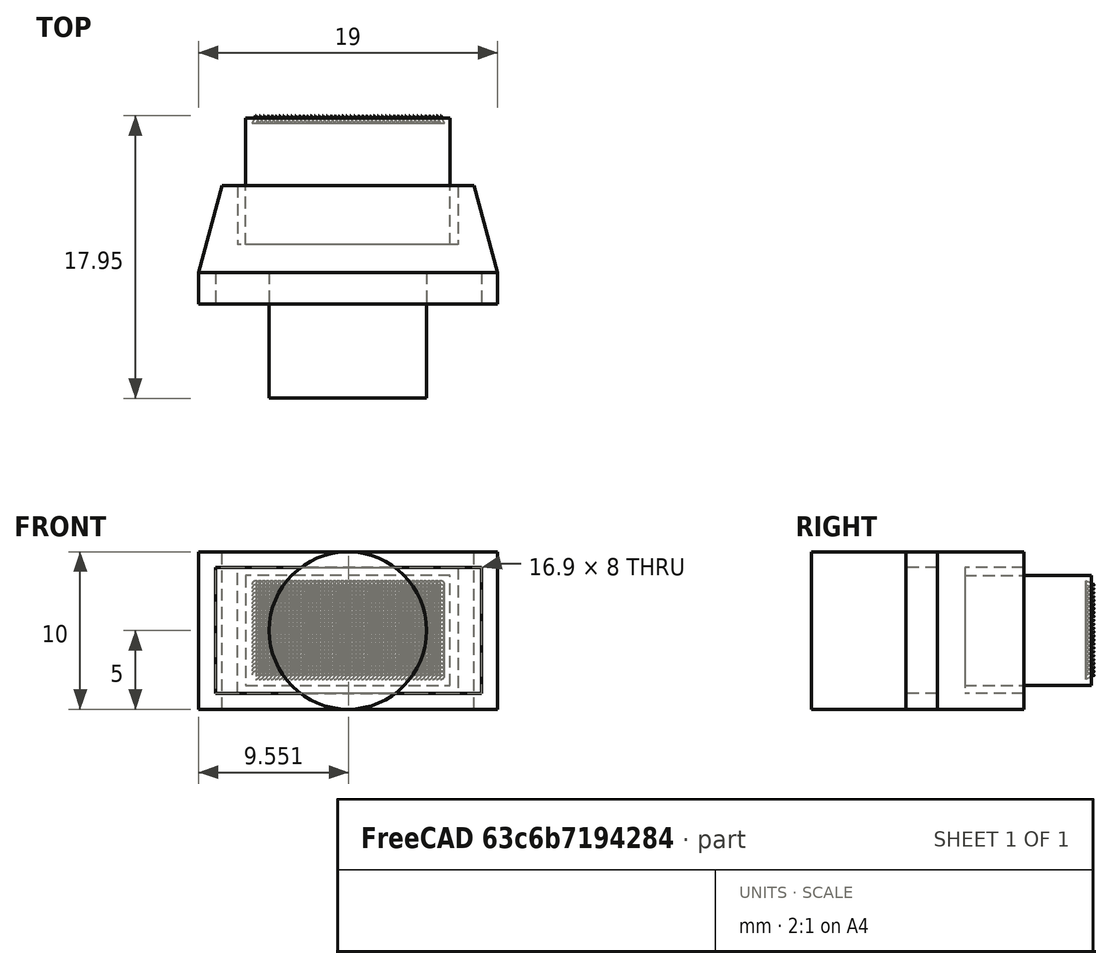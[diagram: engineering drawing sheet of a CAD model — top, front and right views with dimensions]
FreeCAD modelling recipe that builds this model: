
FCSTD DOCUMENT  (FreeCAD 0.18R16110 (Git))
Label: Miyama DS-462
License: All rights reserved
LicenseURL: http://en.wikipedia.org/wiki/All_rights_reserved
objects: Sketcher::SketchObject×8, Part::Extrusion×5, Part::Cut×2, Part::Cone×1, Part::FeaturePython×1, Part::Sweep×1
note: 18 computed .brp shape members not serialized (recipe doc carries the construction recipe); baked Part::Feature solids carry a one-line shape summary decoded from their .brp

FEATURE [Sketcher::SketchObject] Sketch
  sketch-geometry (12):
    g0: LineSegment [constr] StartX=-7 StartY=11.8 StartZ=0 EndX=7 EndY=11.8 EndZ=0
    g1: LineSegment [constr] StartX=-9.5 StartY=0 StartZ=0 EndX=9.5 EndY=0 EndZ=0
    g2: LineSegment [constr] StartX=-7 StartY=11.8 StartZ=0 EndX=-7 EndY=7.5 EndZ=0
    g3: LineSegment [constr] StartX=7 StartY=7.5 StartZ=0 EndX=7 EndY=11.8 EndZ=0
    g4: LineSegment [constr] StartX=9.5 StartY=0 StartZ=0 EndX=9.5 EndY=2 EndZ=0
    g5: LineSegment [constr] StartX=9.5 StartY=2 StartZ=0 EndX=7 EndY=7.5 EndZ=0
    g6: LineSegment [constr] StartX=-9.5 StartY=0 StartZ=0 EndX=-9.5 EndY=2 EndZ=0
    g7: LineSegment [constr] StartX=-9.5 StartY=2 StartZ=0 EndX=-7 EndY=7.5 EndZ=0
    g8: LineSegment StartX=-9.5 StartY=2 StartZ=0 EndX=-9.5 EndY=0 EndZ=0
    g9: LineSegment StartX=-9.5 StartY=0 StartZ=0 EndX=9.5 EndY=0 EndZ=0
    g10: LineSegment StartX=9.5 StartY=0 StartZ=0 EndX=9.5 EndY=2 EndZ=0
    g11: LineSegment StartX=9.5 StartY=2 StartZ=0 EndX=-9.5 EndY=2 EndZ=0
  constraints (31):
    c: DistanceX(g0,g0) = 14
    c: DistanceX(g1,g1) = 19
    c: Symmetric(g0,g0,g-2)
    c: Coincident(g2,g0)
    c: Vertical(g2)
    c: Coincident(g3,g0)
    c: Vertical(g3)
    c: DistanceY(g3,g3) = 4.3
    c: Coincident(g4,g1)
    c: Coincident(g5,g4)
    c: Coincident(g7,g6)
    c: Coincident(g7,g2)
    c: Vertical(g6)
    c: Vertical(g4)
    c: DistanceY(g1,g5) = 7.5
    c: Equal(g4,g6)
    c: Coincident(g6,g1)
    c: DistanceY(g4,g4) = 2
    c: PointOnObject(g-1,g1)
    c: Horizontal(g1)
    c: Equal(g7,g5)
    c: Coincident(g3,g5)
    c: Equal(g3,g2)
    c: Coincident(g6,g8)
    c: Coincident(g8,g1)
    c: Coincident(g8,g9)
    c: Coincident(g9,g1)
    c: Coincident(g9,g10)
    c: Coincident(g10,g4)
    c: Coincident(g10,g11)
    c: Coincident(g11,g8)
FEATURE [Sketcher::SketchObject] Sketch001
  sketch-geometry (12):
    g0: LineSegment [constr] StartX=-8 StartY=11.8 StartZ=0 EndX=8 EndY=11.8 EndZ=0
    g1: LineSegment [constr] StartX=-9.5 StartY=0 StartZ=0 EndX=9.5 EndY=0 EndZ=0
    g2: LineSegment [constr] StartX=-8 StartY=11.8 StartZ=0 EndX=-8 EndY=7.5 EndZ=0
    g3: LineSegment [constr] StartX=8 StartY=7.5 StartZ=0 EndX=8 EndY=11.8 EndZ=0
    g4: LineSegment [constr] StartX=9.5 StartY=0 StartZ=0 EndX=9.5 EndY=2 EndZ=0
    g5: LineSegment [constr] StartX=9.5 StartY=2 StartZ=0 EndX=8 EndY=7.5 EndZ=0
    g6: LineSegment [constr] StartX=-9.5 StartY=0 StartZ=0 EndX=-9.5 EndY=2 EndZ=0
    g7: LineSegment [constr] StartX=-9.5 StartY=2 StartZ=0 EndX=-8 EndY=7.5 EndZ=0
    g8: LineSegment StartX=-9.5 StartY=2 StartZ=0 EndX=-8 EndY=7.5 EndZ=0
    g9: LineSegment StartX=-8 StartY=7.5 StartZ=0 EndX=8 EndY=7.5 EndZ=0
    g10: LineSegment StartX=8 StartY=7.5 StartZ=0 EndX=9.5 EndY=2 EndZ=0
    g11: LineSegment StartX=9.5 StartY=2 StartZ=0 EndX=-9.5 EndY=2 EndZ=0
  constraints (31):
    c: DistanceX(g0,g0) = 16
    c: DistanceX(g1,g1) = 19
    c: Symmetric(g0,g0,g-2)
    c: Coincident(g2,g0)
    c: Vertical(g2)
    c: Coincident(g3,g0)
    c: Vertical(g3)
    c: DistanceY(g3,g3) = 4.3
    c: Coincident(g4,g1)
    c: Coincident(g5,g4)
    c: Coincident(g7,g6)
    c: Coincident(g7,g2)
    c: Vertical(g6)
    c: Vertical(g4)
    c: DistanceY(g1,g5) = 7.5
    c: Equal(g4,g6)
    c: Coincident(g6,g1)
    c: DistanceY(g4,g4) = 2
    c: PointOnObject(g-1,g1)
    c: Horizontal(g1)
    c: Equal(g7,g5)
    c: Coincident(g3,g5)
    c: Equal(g3,g2)
    c: Coincident(g6,g8)
    c: Coincident(g8,g2)
    c: Coincident(g8,g9)
    c: Coincident(g9,g10)
    c: Coincident(g10,g4)
    c: Coincident(g10,g11)
    c: Coincident(g11,g8)
    c: Coincident(g9,g3)
FEATURE [Sketcher::SketchObject] Sketch002
  sketch-geometry (12):
    g0: LineSegment [constr] StartX=-7 StartY=11.8 StartZ=0 EndX=7 EndY=11.8 EndZ=0
    g1: LineSegment [constr] StartX=-9.5 StartY=0 StartZ=0 EndX=9.5 EndY=0 EndZ=0
    g2: LineSegment [constr] StartX=-7 StartY=11.8 StartZ=0 EndX=-7 EndY=7.5 EndZ=0
    g3: LineSegment [constr] StartX=7 StartY=7.5 StartZ=0 EndX=7 EndY=11.8 EndZ=0
    g4: LineSegment [constr] StartX=9.5 StartY=0 StartZ=0 EndX=9.5 EndY=2 EndZ=0
    g5: LineSegment [constr] StartX=9.5 StartY=2 StartZ=0 EndX=7 EndY=7.5 EndZ=0
    g6: LineSegment [constr] StartX=-9.5 StartY=0 StartZ=0 EndX=-9.5 EndY=2 EndZ=0
    g7: LineSegment [constr] StartX=-9.5 StartY=2 StartZ=0 EndX=-7 EndY=7.5 EndZ=0
    g8: LineSegment StartX=-7 StartY=11.8 StartZ=0 EndX=-7 EndY=7.5 EndZ=0
    g9: LineSegment StartX=-7 StartY=7.5 StartZ=0 EndX=7 EndY=7.5 EndZ=0
    g10: LineSegment StartX=7 StartY=7.5 StartZ=0 EndX=7 EndY=11.8 EndZ=0
    g11: LineSegment StartX=7 StartY=11.8 StartZ=0 EndX=-7 EndY=11.8 EndZ=0
  constraints (31):
    c: DistanceX(g0,g0) = 14
    c: DistanceX(g1,g1) = 19
    c: Symmetric(g0,g0,g-2)
    c: Coincident(g2,g0)
    c: Vertical(g2)
    c: Coincident(g3,g0)
    c: Vertical(g3)
    c: DistanceY(g3,g3) = 4.3
    c: Coincident(g4,g1)
    c: Coincident(g5,g4)
    c: Coincident(g7,g6)
    c: Coincident(g7,g2)
    c: Vertical(g6)
    c: Vertical(g4)
    c: DistanceY(g1,g5) = 7.5
    c: Equal(g4,g6)
    c: Coincident(g6,g1)
    c: DistanceY(g4,g4) = 2
    c: PointOnObject(g-1,g1)
    c: Horizontal(g1)
    c: Equal(g7,g5)
    c: Coincident(g3,g5)
    c: Equal(g3,g2)
    c: Coincident(g0,g8)
    c: Coincident(g8,g2)
    c: Coincident(g8,g9)
    c: Coincident(g9,g3)
    c: Coincident(g9,g10)
    c: Coincident(g10,g0)
    c: Coincident(g10,g11)
    c: Coincident(g11,g8)
FEATURE [Part::Extrusion] Extrude
  Base = -> Sketch
  Dir = (0,0,1)
  DirMode = 2
  FaceMakerClass = Part::FaceMakerBullseye
  LengthFwd = 10
  LengthRev = 0
  Solid = true
  Symmetric = false
FEATURE [Part::Extrusion] Extrude001
  Base = -> Sketch001
  Dir = (0,0,1)
  DirMode = 2
  FaceMakerClass = Part::FaceMakerBullseye
  LengthFwd = 10
  LengthRev = 0
  Solid = true
  Symmetric = false
FEATURE [Sketcher::SketchObject] Sketch003
  MapMode = 5
  Placement = pos=(0,7.5,0) rot=(0,0.707107,0.707107;3.14159rad)
  Support = -> [Extrude001]
  sketch-geometry (4):
    g0: LineSegment StartX=-7 StartY=9 StartZ=0 EndX=-7 EndY=1 EndZ=0
    g1: LineSegment StartX=-7 StartY=1 StartZ=0 EndX=7 EndY=1 EndZ=0
    g2: LineSegment StartX=7 StartY=1 StartZ=0 EndX=7 EndY=9 EndZ=0
    g3: LineSegment StartX=7 StartY=9 StartZ=0 EndX=-7 EndY=9 EndZ=0
  constraints (8):
    c: Vertical(g0)
    c: Coincident(g0,g1)
    c: Horizontal(g1)
    c: Coincident(g1,g2)
    c: Vertical(g2)
    c: Coincident(g2,g3)
    c: Coincident(g3,g0)
    c: Horizontal(g3)
FEATURE [Part::Extrusion] Extrude002
  Base = -> Sketch003
  Dir = (0,1,-2e-16)
  DirMode = 2
  FaceMakerClass = Part::FaceMakerBullseye
  LengthFwd = -7.5
  LengthRev = 0
  Solid = true
  Symmetric = true
FEATURE [Part::Cut] Cut
  Base = -> Extrude001
  Tool = -> Extrude002
FEATURE [Sketcher::SketchObject] Sketch004
  MapMode = 5
  Placement = pos=(0,3.75,-8e-16) rot=(0,0.707107,0.707107;3.14159rad)
  Support = -> [Cut]
  sketch-geometry (4):
    g0: LineSegment StartX=-6.5 StartY=8.5 StartZ=0 EndX=6.5 EndY=8.5 EndZ=0
    g1: LineSegment StartX=6.5 StartY=8.5 StartZ=0 EndX=6.5 EndY=1.5 EndZ=0
    g2: LineSegment StartX=6.5 StartY=1.5 StartZ=0 EndX=-6.5 EndY=1.5 EndZ=0
    g3: LineSegment StartX=-6.5 StartY=1.5 StartZ=0 EndX=-6.5 EndY=8.5 EndZ=0
  constraints (8):
    c: Coincident(g0,g1)
    c: Coincident(g1,g2)
    c: Coincident(g2,g3)
    c: Coincident(g3,g0)
    c: Horizontal(g0)
    c: Horizontal(g2)
    c: Vertical(g1)
    c: Vertical(g3)
FEATURE [Part::Extrusion] Extrude003
  Base = -> Sketch004
  Dir = (0,1,-2e-16)
  DirMode = 2
  FaceMakerClass = Part::FaceMakerBullseye
  LengthFwd = 8.05
  LengthRev = 0
  Solid = true
  Symmetric = false
FEATURE [Part::Cone] Cone
  Angle = 360
  AttacherType = Attacher::AttachEngine3D
  Height = 0.5
  Placement = pos=(-5.85,11.45,7.9) rot=(1,0,0;4.71239rad)
  Radius1 = 0.25
  Radius2 = 0.01
FEATURE [Part::FeaturePython] Array  # Draft array (typed FeaturePython)
  Angle = 360
  ArrayType = 0
  Axis = (0,0,1)
  Base = -> Cone
  Center = (0,0,0)
  Fuse = false
  IntervalAxis = (0,0,0)
  IntervalX = (0.25,0,0)
  IntervalY = (0,1,0)
  IntervalZ = (0,0,-0.25)
  NumberPolar = 1
  NumberX = 48
  NumberY = 1
  NumberZ = 24
FEATURE [Sketcher::SketchObject] Sketch005
  MapMode = 5
  Placement = pos=(0,0,0) rot=(1,0,0;1.5708rad)
  Support = -> [Extrude]
  sketch-geometry (4):
    g0: LineSegment StartX=-8.39842 StartY=9 StartZ=0 EndX=8.5 EndY=9 EndZ=0
    g1: LineSegment StartX=8.5 StartY=9 StartZ=0 EndX=8.5 EndY=1 EndZ=0
    g2: LineSegment StartX=8.5 StartY=1 StartZ=0 EndX=-8.39842 EndY=1 EndZ=0
    g3: LineSegment StartX=-8.39842 StartY=1 StartZ=0 EndX=-8.39842 EndY=9 EndZ=0
  constraints (8):
    c: Coincident(g0,g1)
    c: Coincident(g1,g2)
    c: Coincident(g2,g3)
    c: Coincident(g3,g0)
    c: Horizontal(g0)
    c: Horizontal(g2)
    c: Vertical(g1)
    c: Vertical(g3)
FEATURE [Part::Extrusion] Extrude004
  Base = -> Sketch005
  Dir = (0,-1,2e-16)
  DirMode = 2
  FaceMakerClass = Part::FaceMakerBullseye
  LengthFwd = 5
  LengthRev = 0
  Solid = true
  Symmetric = true
FEATURE [Part::Cut] Cut001
  Base = -> Extrude
  Tool = -> Extrude004
FEATURE [Sketcher::SketchObject] Sketch006
  MapMode = 5
  Placement = pos=(0,2,0) rot=(1,0,0;1.5708rad)
  Support = -> [Cut]
  sketch-geometry (1):
    g0: Circle CenterX=0 CenterY=5 CenterZ=0 NormalX=0 NormalY=0 NormalZ=1 AngleXU=0 Radius=5
  constraints (1):
    c: PointOnObject(g0,g-2)
FEATURE [Sketcher::SketchObject] Sketch007
  ExternalGeometry = -> [Cut]
  sketch-geometry (1):
    g0: LineSegment StartX=0 StartY=2.0029 StartZ=0 EndX=0 EndY=-5.9971 EndZ=0
  constraints (1):
    c: DistanceY(g0,g0) = 8
FEATURE [Part::Sweep] Sweep
  Frenet = false
  Sections = -> [Sketch006]
  Solid = true
  Spine = -> Sketch007
  Transition = 1
